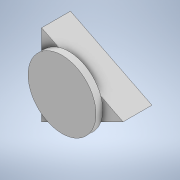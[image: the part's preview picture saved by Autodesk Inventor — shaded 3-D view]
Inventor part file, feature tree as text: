
AUTODESK INVENTOR PART (.ipt)
format: ipt  version: 2020.1 (Build 241239000, 239)  size: 108,544 bytes
history: native  units: mm
features: extrude x2, sketch x2
ambient origin geometry x8: Origin, YZ Plane, XZ Plane, XY Plane, X Axis, Y Axis, Z Axis, Center Point
bodies: Solid1 (feature_tree)
feature tree (4):
  extrude  "Extrusion1"  Depth=10.0mm
  extrude  "Extrusion3"  [1 undecoded]
  sketch  "Sketch1"  dims[d2=4.25mm d3=0.0mm d7=10.0mm]
  sketch  "Sketch2"  dims[d8=1.0mm d9=0.0mm]
note: 1 required parameter value undecoded (feature->parameter linkage not recoverable at this tier; creation-order binding heuristic only, values carry confidence <= 0.55)
